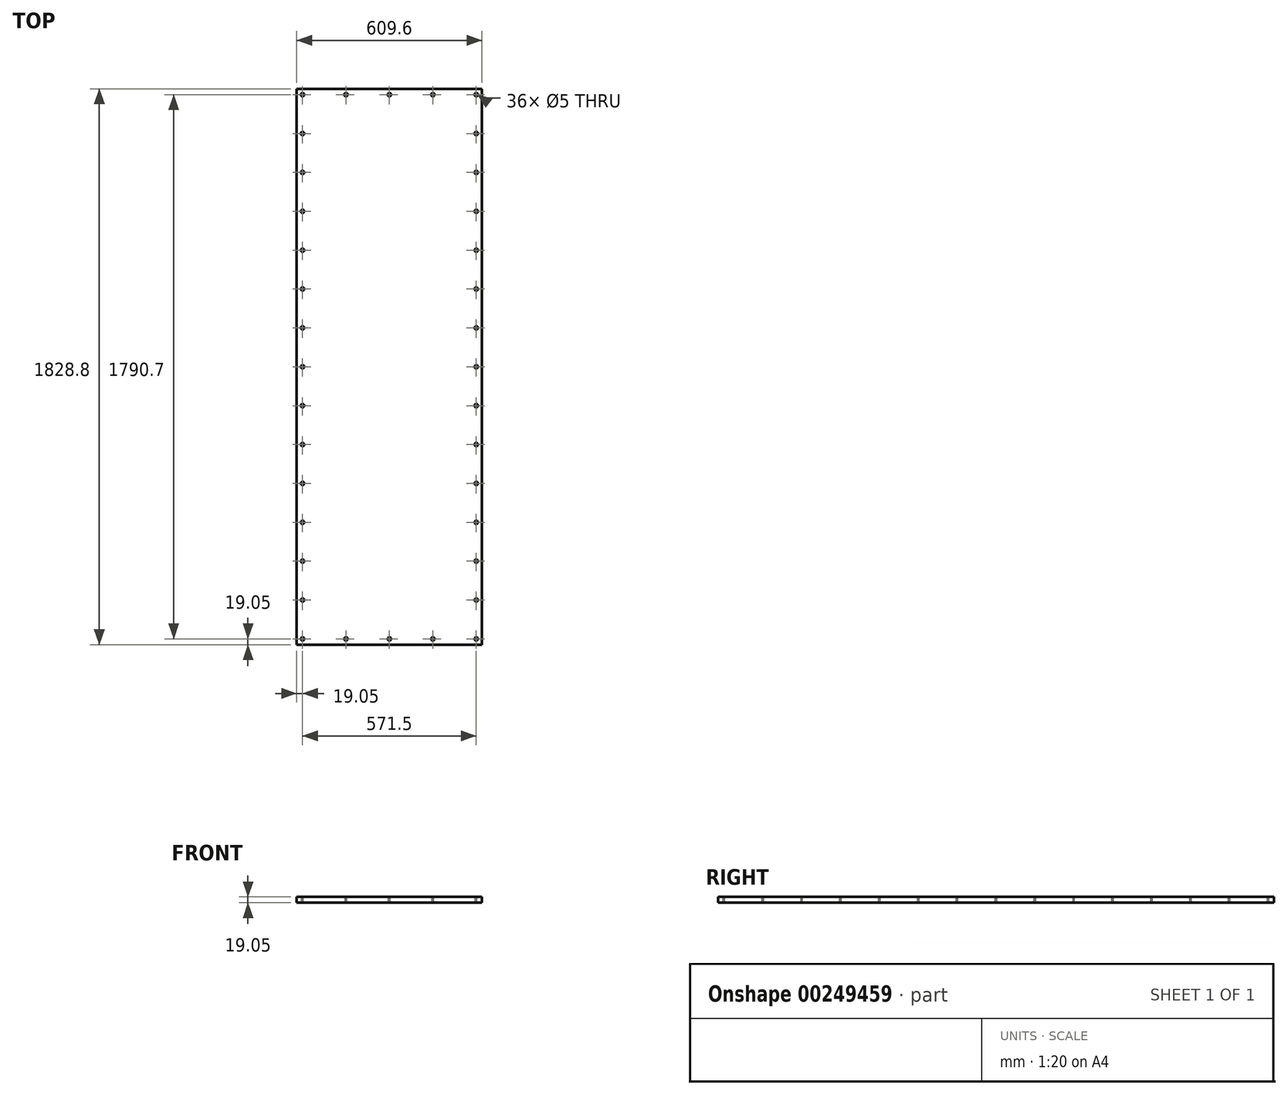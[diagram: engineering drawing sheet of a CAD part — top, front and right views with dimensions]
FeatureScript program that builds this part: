
annotation { "Feature Type Name" : "Feature", "Feature Type Description" : "" }
export const myFeature = defineFeature(function(context is Context, id is Id, definition is map)
    precondition{}
    {
        {
            var Q0;
            Q0=qCreatedBy(makeId("Top.planeOp"),FACE);
            var sketch = newSketch(context, id + "F0", { "sketchPlane" : qUnion([Q0])});
            skLineSegment(sketch, "E0.bottom", {"start": v(0, 0) * mm, "end": v(609.6, 0) * mm});
            skLineSegment(sketch, "E0.top", {"start": v(0, 1828.8) * mm, "end": v(609.6, 1828.8) * mm});
            skLineSegment(sketch, "E0.left", {"start": v(0, 0) * mm, "end": v(0, 1828.8) * mm});
            skLineSegment(sketch, "E0.right", {"start": v(609.6, 0) * mm, "end": v(609.6, 1828.8) * mm});
            skSolve(sketch);
        }
        {
            var Q0;
            Q0 = qSketchRegion(id + "F0", true);
            extrude(context, id + "F1", {"entities" : qUnion([Q0]), "depth" : 19.05 * mm});
        }
        {
            var Q0;
            Q0=makeQuery(id+"F1.opExtrude","CAP_FACE",FACE,{"disambiguationData":[OSD([sQuery(id+"F0.wireOp",EDGE,"E0.bottom"),sQuery(id+"F0.wireOp",EDGE,"E0.top"),sQuery(id+"F0.wireOp",EDGE,"E0.left"),sQuery(id+"F0.wireOp",EDGE,"E0.right")])],"isStart":false});
            var sketch = newSketch(context, id + "F2", { "sketchPlane" : qUnion([Q0])});
            skLineSegment(sketch, "E1", {"start": v(19.05, 914.4) * mm, "end": v(19.05, 1042.3) * mm, "construction": true});
            skLineSegment(sketch, "E2", {"start": v(19.05, 1042.3) * mm, "end": v(19.05, 1170.21) * mm, "construction": true});
            skLineSegment(sketch, "E3", {"start": v(19.05, 1170.21) * mm, "end": v(19.05, 1298.12) * mm, "construction": true});
            skLineSegment(sketch, "E4", {"start": v(19.05, 1298.12) * mm, "end": v(19.05, 1426.03) * mm, "construction": true});
            skLineSegment(sketch, "E5", {"start": v(19.05, 1426.03) * mm, "end": v(19.05, 1553.94) * mm, "construction": true});
            skLineSegment(sketch, "E6", {"start": v(19.05, 1553.94) * mm, "end": v(19.05, 1681.84) * mm, "construction": true});
            skLineSegment(sketch, "E7", {"start": v(19.05, 1681.84) * mm, "end": v(19.05, 1809.75) * mm, "construction": true});
            skLineSegment(sketch, "E8", {"start": v(19.05, 1809.75) * mm, "end": v(161.93, 1809.75) * mm, "construction": true});
            skLineSegment(sketch, "E9", {"start": v(161.93, 1809.75) * mm, "end": v(304.8, 1809.75) * mm, "construction": true});
            skLineSegment(sketch, "E10", {"start": v(304.8, 1828.8) * mm, "end": v(304.8, 0) * mm, "construction": true});
            skLineSegment(sketch, "E11", {"start": v(609.6, 914.4) * mm, "end": v(0, 914.4) * mm, "construction": true});
            skLineSegment(sketch, "E12.MirrorCS", {"start": v(590.55, 1553.94) * mm, "end": v(590.55, 1681.84) * mm, "construction": true});
            skLineSegment(sketch, "E13.MirrorCS", {"start": v(590.55, 1426.03) * mm, "end": v(590.55, 1553.94) * mm, "construction": true});
            skLineSegment(sketch, "E14.MirrorCS", {"start": v(590.55, 914.4) * mm, "end": v(590.55, 1042.3) * mm, "construction": true});
            skLineSegment(sketch, "E15.MirrorCS", {"start": v(590.55, 1298.12) * mm, "end": v(590.55, 1426.03) * mm, "construction": true});
            skLineSegment(sketch, "E16.MirrorCS", {"start": v(590.55, 1809.75) * mm, "end": v(447.68, 1809.75) * mm, "construction": true});
            skLineSegment(sketch, "E17.MirrorCS", {"start": v(590.55, 1042.3) * mm, "end": v(590.55, 1170.21) * mm, "construction": true});
            skLineSegment(sketch, "E18.MirrorCS", {"start": v(447.68, 1809.75) * mm, "end": v(304.8, 1809.75) * mm, "construction": true});
            skLineSegment(sketch, "E19.MirrorCS", {"start": v(590.55, 1681.84) * mm, "end": v(590.55, 1809.75) * mm, "construction": true});
            skLineSegment(sketch, "E20.MirrorCS", {"start": v(590.55, 1170.21) * mm, "end": v(590.55, 1298.12) * mm, "construction": true});
            skLineSegment(sketch, "E21.MirrorCS", {"start": v(161.93, 19.05) * mm, "end": v(304.8, 19.05) * mm, "construction": true});
            skLineSegment(sketch, "E22.MirrorCS", {"start": v(19.05, 658.59) * mm, "end": v(19.05, 530.68) * mm, "construction": true});
            skLineSegment(sketch, "E23.MirrorCS", {"start": v(19.05, 146.96) * mm, "end": v(19.05, 19.05) * mm, "construction": true});
            skLineSegment(sketch, "E24.MirrorCS", {"start": v(19.05, 402.77) * mm, "end": v(19.05, 274.86) * mm, "construction": true});
            skLineSegment(sketch, "E25.MirrorCS", {"start": v(19.05, 786.5) * mm, "end": v(19.05, 658.59) * mm, "construction": true});
            skLineSegment(sketch, "E26.MirrorCS", {"start": v(447.68, 19.05) * mm, "end": v(304.8, 19.05) * mm, "construction": true});
            skLineSegment(sketch, "E27.MirrorCS", {"start": v(19.05, 914.4) * mm, "end": v(19.05, 786.5) * mm, "construction": true});
            skLineSegment(sketch, "E28.MirrorCS", {"start": v(590.55, 786.5) * mm, "end": v(590.55, 658.59) * mm, "construction": true});
            skLineSegment(sketch, "E29.MirrorCS", {"start": v(590.55, 402.77) * mm, "end": v(590.55, 274.86) * mm, "construction": true});
            skLineSegment(sketch, "E30.MirrorCS", {"start": v(19.05, 530.68) * mm, "end": v(19.05, 402.77) * mm, "construction": true});
            skLineSegment(sketch, "E31.MirrorCS", {"start": v(590.55, 146.96) * mm, "end": v(590.55, 19.05) * mm, "construction": true});
            skLineSegment(sketch, "E32.MirrorCS", {"start": v(590.55, 19.05) * mm, "end": v(447.68, 19.05) * mm, "construction": true});
            skLineSegment(sketch, "E33.MirrorCS", {"start": v(590.55, 914.4) * mm, "end": v(590.55, 786.5) * mm, "construction": true});
            skLineSegment(sketch, "E34.MirrorCS", {"start": v(19.05, 274.86) * mm, "end": v(19.05, 146.96) * mm, "construction": true});
            skLineSegment(sketch, "E35.MirrorCS", {"start": v(590.55, 530.68) * mm, "end": v(590.55, 402.77) * mm, "construction": true});
            skLineSegment(sketch, "E36.MirrorCS", {"start": v(590.55, 274.86) * mm, "end": v(590.55, 146.96) * mm, "construction": true});
            skLineSegment(sketch, "E37.MirrorCS", {"start": v(590.55, 658.59) * mm, "end": v(590.55, 530.68) * mm, "construction": true});
            skLineSegment(sketch, "E38.MirrorCS", {"start": v(19.05, 19.05) * mm, "end": v(161.93, 19.05) * mm, "construction": true});
            skSolve(sketch);
        }
        {
            var Q0;
            Q0=sQuery(id+"F2.wireOp",VERTEX,"E8.start");
            var Q1;
            Q1=sQuery(id+"F2.wireOp",VERTEX,"E9.start");
            var Q2;
            Q2=sQuery(id+"F2.wireOp",VERTEX,"E9.end");
            var Q3;
            Q3=sQuery(id+"F2.wireOp",VERTEX,"E18.MirrorCS.start");
            var Q4;
            Q4=sQuery(id+"F2.wireOp",VERTEX,"E19.MirrorCS.end");
            var Q5;
            Q5=sQuery(id+"F2.wireOp",VERTEX,"E19.MirrorCS.start");
            var Q6;
            Q6=sQuery(id+"F2.wireOp",VERTEX,"E12.MirrorCS.start");
            var Q7;
            Q7=sQuery(id+"F2.wireOp",VERTEX,"E15.MirrorCS.end");
            var Q8;
            Q8=sQuery(id+"F2.wireOp",VERTEX,"E20.MirrorCS.start");
            var Q9;
            Q9=sQuery(id+"F2.wireOp",VERTEX,"E14.MirrorCS.end");
            var Q10;
            Q10=sQuery(id+"F2.wireOp",VERTEX,"E14.MirrorCS.start");
            var Q11;
            Q11=sQuery(id+"F2.wireOp",VERTEX,"E15.MirrorCS.start");
            var Q12;
            Q12=sQuery(id+"F2.wireOp",VERTEX,"E28.MirrorCS.start");
            var Q13;
            Q13=sQuery(id+"F2.wireOp",VERTEX,"E37.MirrorCS.start");
            var Q14;
            Q14=sQuery(id+"F2.wireOp",VERTEX,"E35.MirrorCS.start");
            var Q15;
            Q15=sQuery(id+"F2.wireOp",VERTEX,"E29.MirrorCS.start");
            var Q16;
            Q16=sQuery(id+"F2.wireOp",VERTEX,"E36.MirrorCS.start");
            var Q17;
            Q17=sQuery(id+"F2.wireOp",VERTEX,"E31.MirrorCS.start");
            var Q18;
            Q18=sQuery(id+"F2.wireOp",VERTEX,"E31.MirrorCS.end");
            var Q19;
            Q19=sQuery(id+"F2.wireOp",VERTEX,"E26.MirrorCS.start");
            var Q20;
            Q20=sQuery(id+"F2.wireOp",VERTEX,"E26.MirrorCS.end");
            var Q21;
            Q21=sQuery(id+"F2.wireOp",VERTEX,"E21.MirrorCS.start");
            var Q22;
            Q22=sQuery(id+"F2.wireOp",VERTEX,"E23.MirrorCS.end");
            var Q23;
            Q23=sQuery(id+"F2.wireOp",VERTEX,"E23.MirrorCS.start");
            var Q24;
            Q24=sQuery(id+"F2.wireOp",VERTEX,"E34.MirrorCS.start");
            var Q25;
            Q25=sQuery(id+"F2.wireOp",VERTEX,"E24.MirrorCS.start");
            var Q26;
            Q26=sQuery(id+"F2.wireOp",VERTEX,"E30.MirrorCS.start");
            var Q27;
            Q27=sQuery(id+"F2.wireOp",VERTEX,"E22.MirrorCS.start");
            var Q28;
            Q28=sQuery(id+"F2.wireOp",VERTEX,"E27.MirrorCS.end");
            var Q29;
            Q29=sQuery(id+"F2.wireOp",VERTEX,"E27.MirrorCS.start");
            var Q30;
            Q30=sQuery(id+"F2.wireOp",VERTEX,"E2.start");
            var Q31;
            Q31=sQuery(id+"F2.wireOp",VERTEX,"E3.start");
            var Q32;
            Q32=sQuery(id+"F2.wireOp",VERTEX,"E4.start");
            var Q33;
            Q33=sQuery(id+"F2.wireOp",VERTEX,"E5.start");
            var Q34;
            Q34=sQuery(id+"F2.wireOp",VERTEX,"E6.start");
            var Q35;
            Q35=sQuery(id+"F2.wireOp",VERTEX,"E7.start");
            var Q36;
            Q36=makeQuery(id+"F1.opExtrude","SWEPT_BODY",BODY,{"disambiguationData":[OSD([sQuery(id+"F0.wireOp",EDGE,"E0.bottom"),sQuery(id+"F0.wireOp",EDGE,"E0.top"),sQuery(id+"F0.wireOp",EDGE,"E0.left"),sQuery(id+"F0.wireOp",EDGE,"E0.right")])]});
            hole(context, id + "F3", {"style" : HoleStyle.C_SINK, "endStyle" : HoleEndStyle.THROUGH, "standardTappedOrClearance" : lookupTablePath({ "standard" : "ISO", "size" : "5", "type" : "Drilled" }), "standardBlindInLast" : lookupTablePath({ "standard" : "ISO", "size" : "5", "type" : "Drilled" }), "holeDiameter" : 5 * mm, "cSinkDiameter" : 11.2 * mm, "cSinkAngle" : 90 * degree, "tappedDepth" : 12.7 * mm, "tapClearance" : 3, "startFromSketch" : true, "locations" : qUnion([Q0, Q1, Q2, Q3, Q4, Q5, Q6, Q7, Q8, Q9, Q10, Q11, Q12, Q13, Q14, Q15, Q16, Q17, Q18, Q19, Q20, Q21, Q22, Q23, Q24, Q25, Q26, Q27, Q28, Q29, Q30, Q31, Q32, Q33, Q34, Q35]), "scope" : qUnion([Q36])});
        }
    });
